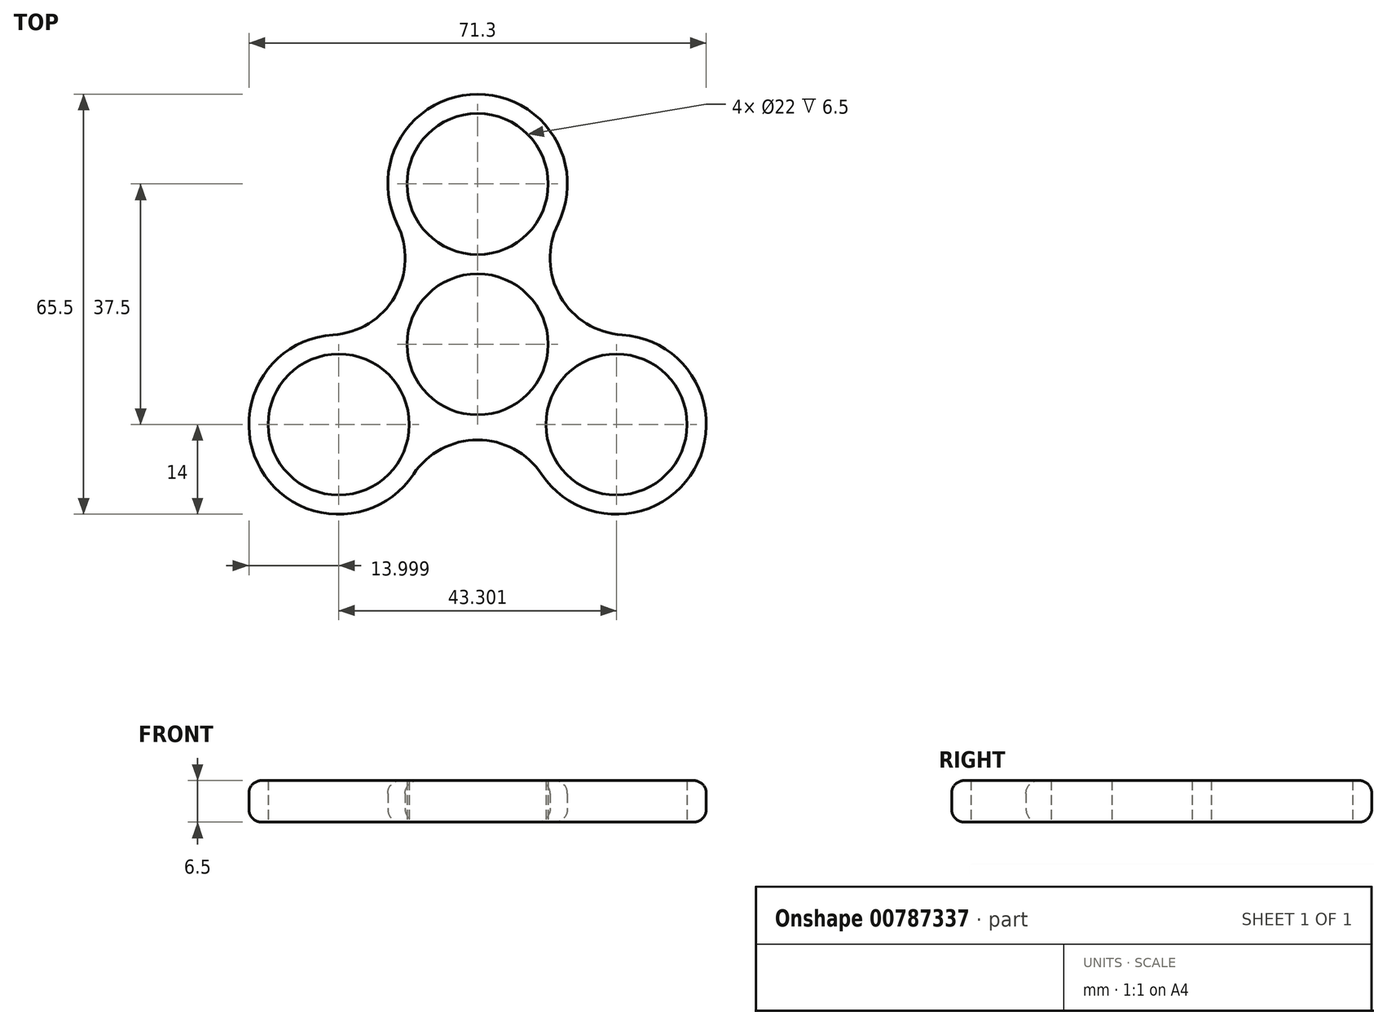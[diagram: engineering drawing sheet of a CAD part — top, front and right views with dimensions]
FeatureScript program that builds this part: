
annotation { "Feature Type Name" : "Feature", "Feature Type Description" : "" }
export const myFeature = defineFeature(function(context is Context, id is Id, definition is map)
    precondition{}
    {
        {
            var Q0;
            Q0=qCreatedBy(makeId("Top.planeOp"),FACE);
            var sketch = newSketch(context, id + "F0", { "sketchPlane" : qUnion([Q0])});
            skCircle(sketch, "E0", {"center": v(0, 0) * mm, "radius": 11 * mm});
            skCircle(sketch, "E1", {"center": v(0, 0) * mm, "radius": 16.5 * mm});
            skCircle(sketch, "E2", {"center": v(0, 25) * mm, "radius": 11 * mm});
            skCircle(sketch, "E3", {"center": v(0, 25) * mm, "radius": 14 * mm});
            skLineSegment(sketch, "E4", {"start": v(0, 0) * mm, "end": v(-33.5, -19.34) * mm, "construction": true});
            skLineSegment(sketch, "E5", {"start": v(35.5, -20.5) * mm, "end": v(0, 0) * mm, "construction": true});
            skLineSegment(sketch, "E6", {"start": v(0, 0) * mm, "end": v(54.09, 31.23) * mm, "construction": true});
            skCircle(sketch, "E7", {"center": v(23.3, 13.45) * mm, "radius": 12 * mm});
            skCircle(sketch, "E8", {"center": v(0, 0) * mm, "radius": 38 * mm});
            skCircle(sketch, "E9.1.0", {"center": v(-23.3, 13.45) * mm, "radius": 12 * mm});
            skCircle(sketch, "E9.2.0", {"center": v(0, -26.9) * mm, "radius": 12 * mm});
            skCircle(sketch, "E10.1.0", {"center": v(-21.65, -12.5) * mm, "radius": 14 * mm});
            skCircle(sketch, "E10.1.1", {"center": v(-21.65, -12.5) * mm, "radius": 11 * mm});
            skCircle(sketch, "E10.2.0", {"center": v(21.65, -12.5) * mm, "radius": 14 * mm});
            skCircle(sketch, "E10.2.1", {"center": v(21.65, -12.5) * mm, "radius": 11 * mm});
            skSolve(sketch);
        }
        {
            var Q0;
            {var subQ0=sQuery(id+"F0.wireOp",EDGE,"E8");var subQ1=sQuery(id+"F0.wireOp",EDGE,"E3");var subQ2=makeQuery(id+"F0.imprint","INTERSECT",VERTEX,{"disambiguationData":[OD(0.0)],"derivedFrom":[subQ1,subQ0]});Q0=makeQuery(id+"F0.imprint","IMPRINT",FACE,{"disambiguationData":[TD([[makeQuery(id+"F0.imprint","IMPRINT",EDGE,{"disambiguationData":[TD([[subQ2,-1.0]])],"derivedFrom":subQ1}),1.0]])]});}
            var Q1;
            {var subQ1=sQuery(id+"F0.wireOp",EDGE,"E3");var subQ6=sQuery(id+"F0.wireOp",EDGE,"E1");var subQ11=makeQuery(id+"F0.imprint","INTERSECT",VERTEX,{"disambiguationData":[OD(0.0)],"derivedFrom":[subQ6,subQ1]});Q1=makeQuery(id+"F0.imprint","IMPRINT",FACE,{"disambiguationData":[TD([[makeQuery(id+"F0.imprint","IMPRINT",EDGE,{"disambiguationData":[TD([[subQ11,-1.0]])],"derivedFrom":subQ6}),-1.0]])]});}
            var Q2;
            {var subQ0=sQuery(id+"F0.wireOp",EDGE,"E9.1.0");var subQ1=sQuery(id+"F0.wireOp",EDGE,"E3");var subQ2=makeQuery(id+"F0.imprint","INTERSECT",VERTEX,{"disambiguationData":[OD(0.0)],"derivedFrom":[subQ1,subQ0]});Q2=makeQuery(id+"F0.imprint","IMPRINT",FACE,{"disambiguationData":[TD([[makeQuery(id+"F0.imprint","IMPRINT",EDGE,{"disambiguationData":[TD([[subQ2,-1.0]])],"derivedFrom":subQ1}),1.0]])]});}
            var Q3;
            {var subQ0=sQuery(id+"F0.wireOp",EDGE,"E7");var subQ1=sQuery(id+"F0.wireOp",EDGE,"E3");var subQ2=makeQuery(id+"F0.imprint","INTERSECT",VERTEX,{"disambiguationData":[OD(0.0)],"derivedFrom":[subQ1,subQ0]});Q3=makeQuery(id+"F0.imprint","IMPRINT",FACE,{"disambiguationData":[TD([[makeQuery(id+"F0.imprint","IMPRINT",EDGE,{"disambiguationData":[TD([[subQ2,1.0]])],"derivedFrom":subQ1}),1.0]])]});}
            var Q4;
            {var subQ4=sQuery(id+"F0.wireOp",EDGE,"E3");var subQ7=sQuery(id+"F0.wireOp",EDGE,"E0");var subQ8=makeQuery(id+"F0.imprint","INTERSECT",VERTEX,{"disambiguationData":[OD(0.0)],"derivedFrom":[subQ7,subQ4]});Q4=makeQuery(id+"F0.imprint","IMPRINT",FACE,{"disambiguationData":[TD([[makeQuery(id+"F0.imprint","IMPRINT",EDGE,{"disambiguationData":[TD([[subQ8,-1.0]])],"derivedFrom":subQ7}),-1.0]])]});}
            var Q5;
            {var subQ0=sQuery(id+"F0.wireOp",EDGE,"E3");var subQ1=sQuery(id+"F0.wireOp",EDGE,"E0");var subQ2=makeQuery(id+"F0.imprint","INTERSECT",VERTEX,{"disambiguationData":[OD(1.0)],"derivedFrom":[subQ1,subQ0]});Q5=makeQuery(id+"F0.imprint","IMPRINT",FACE,{"disambiguationData":[TD([[makeQuery(id+"F0.imprint","IMPRINT",EDGE,{"disambiguationData":[TD([[subQ2,-1.0]])],"derivedFrom":subQ1}),-1.0]])]});}
            var Q6;
            {var subQ0=sQuery(id+"F0.wireOp",EDGE,"E3");var subQ1=sQuery(id+"F0.wireOp",EDGE,"E0");var subQ2=makeQuery(id+"F0.imprint","INTERSECT",VERTEX,{"disambiguationData":[OD(0.0)],"derivedFrom":[subQ1,subQ0]});Q6=makeQuery(id+"F0.imprint","IMPRINT",FACE,{"disambiguationData":[TD([[makeQuery(id+"F0.imprint","IMPRINT",EDGE,{"disambiguationData":[TD([[subQ2,1.0]])],"derivedFrom":subQ1}),-1.0]])]});}
            var Q7;
            {var subQ0=sQuery(id+"F0.wireOp",EDGE,"E10.2.0");var subQ1=sQuery(id+"F0.wireOp",EDGE,"E0");var subQ2=makeQuery(id+"F0.imprint","INTERSECT",VERTEX,{"disambiguationData":[OD(0.0)],"derivedFrom":[subQ1,subQ0]});Q7=makeQuery(id+"F0.imprint","IMPRINT",FACE,{"disambiguationData":[TD([[makeQuery(id+"F0.imprint","IMPRINT",EDGE,{"disambiguationData":[TD([[subQ2,1.0]])],"derivedFrom":subQ1}),-1.0]])]});}
            var Q8;
            {var subQ0=sQuery(id+"F0.wireOp",EDGE,"E10.1.0");var subQ1=sQuery(id+"F0.wireOp",EDGE,"E0");var subQ2=makeQuery(id+"F0.imprint","INTERSECT",VERTEX,{"disambiguationData":[OD(1.0)],"derivedFrom":[subQ1,subQ0]});Q8=makeQuery(id+"F0.imprint","IMPRINT",FACE,{"disambiguationData":[TD([[makeQuery(id+"F0.imprint","IMPRINT",EDGE,{"disambiguationData":[TD([[subQ2,-1.0]])],"derivedFrom":subQ1}),-1.0]])]});}
            var Q9;
            {var subQ0=sQuery(id+"F0.wireOp",EDGE,"E10.1.0");var subQ1=sQuery(id+"F0.wireOp",EDGE,"E0");var subQ9=makeQuery(id+"F0.imprint","INTERSECT",VERTEX,{"disambiguationData":[OD(0.0)],"derivedFrom":[subQ1,subQ0]});Q9=makeQuery(id+"F0.imprint","IMPRINT",FACE,{"disambiguationData":[TD([[makeQuery(id+"F0.imprint","IMPRINT",EDGE,{"disambiguationData":[TD([[subQ9,-1.0]])],"derivedFrom":subQ1}),-1.0]])]});}
            var Q10;
            {var subQ0=sQuery(id+"F0.wireOp",EDGE,"E10.1.0");var subQ7=sQuery(id+"F0.wireOp",EDGE,"E1");var subQ14=makeQuery(id+"F0.imprint","INTERSECT",VERTEX,{"disambiguationData":[OD(0.0)],"derivedFrom":[subQ7,subQ0]});Q10=makeQuery(id+"F0.imprint","IMPRINT",FACE,{"disambiguationData":[TD([[makeQuery(id+"F0.imprint","IMPRINT",EDGE,{"disambiguationData":[TD([[subQ14,-1.0]])],"derivedFrom":subQ7}),-1.0]])]});}
            var Q11;
            {var subQ0=sQuery(id+"F0.wireOp",EDGE,"E10.1.0");var subQ1=sQuery(id+"F0.wireOp",EDGE,"E8");var subQ2=makeQuery(id+"F0.imprint","INTERSECT",VERTEX,{"disambiguationData":[OD(0.0)],"derivedFrom":[subQ1,subQ0]});Q11=makeQuery(id+"F0.imprint","IMPRINT",FACE,{"disambiguationData":[TD([[makeQuery(id+"F0.imprint","IMPRINT",EDGE,{"disambiguationData":[TD([[subQ2,-1.0]])],"derivedFrom":subQ1}),-1.0]])]});}
            var Q12;
            {var subQ0=sQuery(id+"F0.wireOp",EDGE,"E10.2.0");var subQ7=sQuery(id+"F0.wireOp",EDGE,"E1");var subQ15=makeQuery(id+"F0.imprint","INTERSECT",VERTEX,{"disambiguationData":[OD(1.0)],"derivedFrom":[subQ7,subQ0]});Q12=makeQuery(id+"F0.imprint","IMPRINT",FACE,{"disambiguationData":[TD([[makeQuery(id+"F0.imprint","IMPRINT",EDGE,{"disambiguationData":[TD([[subQ15,-1.0]])],"derivedFrom":subQ7}),-1.0]])]});}
            var Q13;
            {var subQ0=sQuery(id+"F0.wireOp",EDGE,"E10.2.0");var subQ1=sQuery(id+"F0.wireOp",EDGE,"E8");var subQ2=makeQuery(id+"F0.imprint","INTERSECT",VERTEX,{"disambiguationData":[OD(0.0)],"derivedFrom":[subQ1,subQ0]});Q13=makeQuery(id+"F0.imprint","IMPRINT",FACE,{"disambiguationData":[TD([[makeQuery(id+"F0.imprint","IMPRINT",EDGE,{"disambiguationData":[TD([[subQ2,-1.0]])],"derivedFrom":subQ1}),-1.0]])]});}
            var Q14;
            {var subQ0=sQuery(id+"F0.wireOp",EDGE,"E3");var subQ1=sQuery(id+"F0.wireOp",EDGE,"E1");var subQ2=makeQuery(id+"F0.imprint","INTERSECT",VERTEX,{"disambiguationData":[OD(0.0)],"derivedFrom":[subQ1,subQ0]});Q14=makeQuery(id+"F0.imprint","IMPRINT",FACE,{"disambiguationData":[TD([[makeQuery(id+"F0.imprint","IMPRINT",EDGE,{"disambiguationData":[TD([[subQ2,1.0]])],"derivedFrom":subQ1}),-1.0]])]});}
            var Q15;
            {var subQ0=sQuery(id+"F0.wireOp",EDGE,"E3");var subQ1=sQuery(id+"F0.wireOp",EDGE,"E1");var subQ2=makeQuery(id+"F0.imprint","INTERSECT",VERTEX,{"disambiguationData":[OD(1.0)],"derivedFrom":[subQ1,subQ0]});Q15=makeQuery(id+"F0.imprint","IMPRINT",FACE,{"disambiguationData":[TD([[makeQuery(id+"F0.imprint","IMPRINT",EDGE,{"disambiguationData":[TD([[subQ2,-1.0]])],"derivedFrom":subQ1}),-1.0]])]});}
            var Q16;
            {var subQ0=sQuery(id+"F0.wireOp",EDGE,"E10.1.0");var subQ1=sQuery(id+"F0.wireOp",EDGE,"E1");var subQ2=makeQuery(id+"F0.imprint","INTERSECT",VERTEX,{"disambiguationData":[OD(1.0)],"derivedFrom":[subQ1,subQ0]});Q16=makeQuery(id+"F0.imprint","IMPRINT",FACE,{"disambiguationData":[TD([[makeQuery(id+"F0.imprint","IMPRINT",EDGE,{"disambiguationData":[TD([[subQ2,-1.0]])],"derivedFrom":subQ1}),-1.0]])]});}
            var Q17;
            {var subQ0=sQuery(id+"F0.wireOp",EDGE,"E8");var subQ1=sQuery(id+"F0.wireOp",EDGE,"E3");var subQ2=makeQuery(id+"F0.imprint","INTERSECT",VERTEX,{"disambiguationData":[OD(0.0)],"derivedFrom":[subQ1,subQ0]});Q17=makeQuery(id+"F0.imprint","IMPRINT",FACE,{"disambiguationData":[TD([[makeQuery(id+"F0.imprint","IMPRINT",EDGE,{"disambiguationData":[TD([[subQ2,1.0]])],"derivedFrom":subQ1}),1.0]])]});}
            var Q18;
            {var subQ0=sQuery(id+"F0.wireOp",EDGE,"E10.1.0");var subQ2=sQuery(id+"F0.wireOp",EDGE,"E1");var subQ4=makeQuery(id+"F0.imprint","INTERSECT",VERTEX,{"disambiguationData":[OD(0.0)],"derivedFrom":[subQ2,subQ0]});Q18=makeQuery(id+"F0.imprint","IMPRINT",FACE,{"disambiguationData":[TD([[makeQuery(id+"F0.imprint","IMPRINT",EDGE,{"disambiguationData":[TD([[subQ4,-1.0]])],"derivedFrom":subQ2}),1.0]])]});}
            var Q19;
            {var subQ1=sQuery(id+"F0.wireOp",EDGE,"E1");var subQ3=sQuery(id+"F0.wireOp",EDGE,"E3");var subQ7=makeQuery(id+"F0.imprint","INTERSECT",VERTEX,{"disambiguationData":[OD(0.0)],"derivedFrom":[subQ1,subQ3]});Q19=makeQuery(id+"F0.imprint","IMPRINT",FACE,{"disambiguationData":[TD([[makeQuery(id+"F0.imprint","IMPRINT",EDGE,{"disambiguationData":[TD([[subQ7,-1.0]])],"derivedFrom":subQ1}),1.0]])]});}
            var Q20;
            {var subQ0=sQuery(id+"F0.wireOp",EDGE,"E10.2.0");var subQ2=sQuery(id+"F0.wireOp",EDGE,"E1");var subQ6=makeQuery(id+"F0.imprint","INTERSECT",VERTEX,{"disambiguationData":[OD(1.0)],"derivedFrom":[subQ2,subQ0]});Q20=makeQuery(id+"F0.imprint","IMPRINT",FACE,{"disambiguationData":[TD([[makeQuery(id+"F0.imprint","IMPRINT",EDGE,{"disambiguationData":[TD([[subQ6,-1.0]])],"derivedFrom":subQ2}),1.0]])]});}
            var Q21;
            {var subQ0=sQuery(id+"F0.wireOp",EDGE,"E7");var subQ1=sQuery(id+"F0.wireOp",EDGE,"E1");var subQ2=makeQuery(id+"F0.imprint","INTERSECT",VERTEX,{"disambiguationData":[OD(0.0)],"derivedFrom":[subQ1,subQ0]});Q21=makeQuery(id+"F0.imprint","IMPRINT",FACE,{"disambiguationData":[TD([[makeQuery(id+"F0.imprint","IMPRINT",EDGE,{"disambiguationData":[TD([[subQ2,1.0]])],"derivedFrom":subQ1}),-1.0]])]});}
            var Q22;
            {var subQ0=sQuery(id+"F0.wireOp",EDGE,"E9.1.0");var subQ1=sQuery(id+"F0.wireOp",EDGE,"E1");var subQ2=makeQuery(id+"F0.imprint","INTERSECT",VERTEX,{"disambiguationData":[OD(1.0)],"derivedFrom":[subQ1,subQ0]});Q22=makeQuery(id+"F0.imprint","IMPRINT",FACE,{"disambiguationData":[TD([[makeQuery(id+"F0.imprint","IMPRINT",EDGE,{"disambiguationData":[TD([[subQ2,-1.0]])],"derivedFrom":subQ1}),-1.0]])]});}
            var Q23;
            {var subQ0=sQuery(id+"F0.wireOp",EDGE,"E9.2.0");var subQ1=sQuery(id+"F0.wireOp",EDGE,"E1");var subQ2=makeQuery(id+"F0.imprint","INTERSECT",VERTEX,{"disambiguationData":[OD(1.0)],"derivedFrom":[subQ1,subQ0]});Q23=makeQuery(id+"F0.imprint","IMPRINT",FACE,{"disambiguationData":[TD([[makeQuery(id+"F0.imprint","IMPRINT",EDGE,{"disambiguationData":[TD([[subQ2,-1.0]])],"derivedFrom":subQ1}),-1.0]])]});}
            extrude(context, id + "F1", {"entities" : qUnion([Q0, Q1, Q2, Q3, Q4, Q5, Q6, Q7, Q8, Q9, Q10, Q11, Q12, Q13, Q14, Q15, Q16, Q17, Q18, Q19, Q20, Q21, Q22, Q23]), "depth" : 6.5 * mm, "offsetDistance" : 25 * mm});
        }
        {
            var Q0;
            {var subQ0=sQuery(id+"F0.wireOp",EDGE,"E3");Q0=makeQuery(id+"F1.opExtrude","CAP_EDGE",EDGE,{"disambiguationData":[OSD([subQ0]),TDD([makeQuery(id+"F0.imprint","IMPRINT",EDGE,{"disambiguationData":[TD([[makeQuery(id+"F0.imprint","INTERSECT",VERTEX,{"disambiguationData":[OD(1.0)],"derivedFrom":[sQuery(id+"F0.wireOp",EDGE,"E1"),subQ0]}),1.0]])],"derivedFrom":subQ0})])],"isStart":false});}
            var Q1;
            {var subQ0=sQuery(id+"F0.wireOp",EDGE,"E3");Q1=makeQuery(id+"F1.opExtrude","CAP_EDGE",EDGE,{"disambiguationData":[OSD([subQ0]),TDD([makeQuery(id+"F0.imprint","IMPRINT",EDGE,{"disambiguationData":[TD([[makeQuery(id+"F0.imprint","INTERSECT",VERTEX,{"disambiguationData":[OD(0.0)],"derivedFrom":[sQuery(id+"F0.wireOp",EDGE,"E1"),subQ0]}),-1.0]])],"derivedFrom":subQ0})])],"isStart":false});}
            var Q2;
            {var subQ0=sQuery(id+"F0.wireOp",EDGE,"9b9f4797-2515-45a0-b8ed-e6205bdc4525.2.1");Q2=makeQuery(id+"F1.opExtrude","CAP_EDGE",EDGE,{"disambiguationData":[OSD([subQ0]),TDD([makeQuery(id+"F0.imprint","IMPRINT",EDGE,{"disambiguationData":[TD([[makeQuery(id+"F0.imprint","INTERSECT",VERTEX,{"disambiguationData":[OD(0.0)],"derivedFrom":[sQuery(id+"F0.wireOp",EDGE,"E1"),subQ0]}),1.0]])],"derivedFrom":subQ0})])],"isStart":false});}
            var Q3;
            {var subQ0=sQuery(id+"F0.wireOp",EDGE,"9b9f4797-2515-45a0-b8ed-e6205bdc4525.1.1");Q3=makeQuery(id+"F1.opExtrude","CAP_EDGE",EDGE,{"disambiguationData":[OSD([subQ0]),TDD([makeQuery(id+"F0.imprint","IMPRINT",EDGE,{"disambiguationData":[TD([[makeQuery(id+"F0.imprint","INTERSECT",VERTEX,{"disambiguationData":[OD(0.0)],"derivedFrom":[sQuery(id+"F0.wireOp",EDGE,"E1"),subQ0]}),-1.0]])],"derivedFrom":subQ0})])],"isStart":false});}
            var Q4;
            {var subQ0=sQuery(id+"F0.wireOp",EDGE,"9b9f4797-2515-45a0-b8ed-e6205bdc4525.1.1");Q4=makeQuery(id+"F1.opExtrude","CAP_EDGE",EDGE,{"disambiguationData":[OSD([subQ0]),TDD([makeQuery(id+"F0.imprint","IMPRINT",EDGE,{"disambiguationData":[TD([[makeQuery(id+"F0.imprint","INTERSECT",VERTEX,{"disambiguationData":[OD(1.0)],"derivedFrom":[sQuery(id+"F0.wireOp",EDGE,"E1"),subQ0]}),1.0]])],"derivedFrom":subQ0})])],"isStart":false});}
            var Q5;
            {var subQ0=sQuery(id+"F0.wireOp",EDGE,"9b9f4797-2515-45a0-b8ed-e6205bdc4525.2.1");Q5=makeQuery(id+"F1.opExtrude","CAP_EDGE",EDGE,{"disambiguationData":[OSD([subQ0]),TDD([makeQuery(id+"F0.imprint","IMPRINT",EDGE,{"disambiguationData":[TD([[makeQuery(id+"F0.imprint","INTERSECT",VERTEX,{"disambiguationData":[OD(1.0)],"derivedFrom":[sQuery(id+"F0.wireOp",EDGE,"E1"),subQ0]}),-1.0]])],"derivedFrom":subQ0})])],"isStart":false});}
            var Q6;
            {var subQ0=sQuery(id+"F0.wireOp",EDGE,"9b9f4797-2515-45a0-b8ed-e6205bdc4525.1.1");Q6=makeQuery(id+"F1.opExtrude","CAP_EDGE",EDGE,{"disambiguationData":[OSD([subQ0]),TDD([makeQuery(id+"F0.imprint","IMPRINT",EDGE,{"disambiguationData":[TD([[makeQuery(id+"F0.imprint","INTERSECT",VERTEX,{"disambiguationData":[OD(1.0)],"derivedFrom":[sQuery(id+"F0.wireOp",EDGE,"E1"),subQ0]}),1.0]])],"derivedFrom":subQ0})])],"isStart":true});}
            var Q7;
            {var subQ0=sQuery(id+"F0.wireOp",EDGE,"9b9f4797-2515-45a0-b8ed-e6205bdc4525.2.1");Q7=makeQuery(id+"F1.opExtrude","CAP_EDGE",EDGE,{"disambiguationData":[OSD([subQ0]),TDD([makeQuery(id+"F0.imprint","IMPRINT",EDGE,{"disambiguationData":[TD([[makeQuery(id+"F0.imprint","INTERSECT",VERTEX,{"disambiguationData":[OD(1.0)],"derivedFrom":[sQuery(id+"F0.wireOp",EDGE,"E1"),subQ0]}),-1.0]])],"derivedFrom":subQ0})])],"isStart":true});}
            var Q8;
            {var subQ0=sQuery(id+"F0.wireOp",EDGE,"9b9f4797-2515-45a0-b8ed-e6205bdc4525.1.1");Q8=makeQuery(id+"F1.opExtrude","CAP_EDGE",EDGE,{"disambiguationData":[OSD([subQ0]),TDD([makeQuery(id+"F0.imprint","IMPRINT",EDGE,{"disambiguationData":[TD([[makeQuery(id+"F0.imprint","INTERSECT",VERTEX,{"disambiguationData":[OD(0.0)],"derivedFrom":[sQuery(id+"F0.wireOp",EDGE,"E1"),subQ0]}),-1.0]])],"derivedFrom":subQ0})])],"isStart":true});}
            var Q9;
            {var subQ0=sQuery(id+"F0.wireOp",EDGE,"E3");Q9=makeQuery(id+"F1.opExtrude","CAP_EDGE",EDGE,{"disambiguationData":[OSD([subQ0]),TDD([makeQuery(id+"F0.imprint","IMPRINT",EDGE,{"disambiguationData":[TD([[makeQuery(id+"F0.imprint","INTERSECT",VERTEX,{"disambiguationData":[OD(1.0)],"derivedFrom":[sQuery(id+"F0.wireOp",EDGE,"E1"),subQ0]}),1.0]])],"derivedFrom":subQ0})])],"isStart":true});}
            var Q10;
            {var subQ0=sQuery(id+"F0.wireOp",EDGE,"E3");Q10=makeQuery(id+"F1.opExtrude","CAP_EDGE",EDGE,{"disambiguationData":[OSD([subQ0]),TDD([makeQuery(id+"F0.imprint","IMPRINT",EDGE,{"disambiguationData":[TD([[makeQuery(id+"F0.imprint","INTERSECT",VERTEX,{"disambiguationData":[OD(0.0)],"derivedFrom":[sQuery(id+"F0.wireOp",EDGE,"E1"),subQ0]}),-1.0]])],"derivedFrom":subQ0})])],"isStart":true});}
            var Q11;
            {var subQ0=sQuery(id+"F0.wireOp",EDGE,"9b9f4797-2515-45a0-b8ed-e6205bdc4525.2.1");Q11=makeQuery(id+"F1.opExtrude","CAP_EDGE",EDGE,{"disambiguationData":[OSD([subQ0]),TDD([makeQuery(id+"F0.imprint","IMPRINT",EDGE,{"disambiguationData":[TD([[makeQuery(id+"F0.imprint","INTERSECT",VERTEX,{"disambiguationData":[OD(0.0)],"derivedFrom":[sQuery(id+"F0.wireOp",EDGE,"E1"),subQ0]}),1.0]])],"derivedFrom":subQ0})])],"isStart":true});}
            fillet(context, id + "F2", {"entities" : qUnion([Q0, Q1, Q2, Q3, Q4, Q5, Q6, Q7, Q8, Q9, Q10, Q11]), "radius" : 2 * mm, "tangentPropagation" : true, "allowEdgeOverflow" : false});
        }
    });
